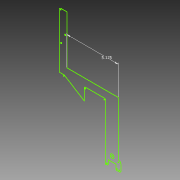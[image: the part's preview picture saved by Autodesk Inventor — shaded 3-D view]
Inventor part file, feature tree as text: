
AUTODESK INVENTOR PART (.ipt)
format: ipt  version: 2013 (Build 170138000, 138)  size: 66,048 bytes
history: native  units: in
note: dims shown in document units (in); Inventor stores cm internally (conversion verified against a paired STEP export)
features: sketch x1
ambient origin geometry x8: Origin, YZ Plane, XZ Plane, XY Plane, X Axis, Y Axis, Z Axis, Center Point
feature tree (1):
  sketch  "Sketch1"  dims[d0=5.125in]
